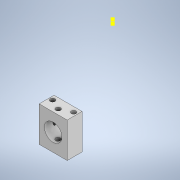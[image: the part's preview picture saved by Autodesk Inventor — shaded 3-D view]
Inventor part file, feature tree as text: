
AUTODESK INVENTOR PART (.ipt)
format: ipt  version: 2022 (Build 260153000, 153)  size: 735,744 bytes
history: native  units: in
note: dims shown in document units (in); Inventor stores cm internally (conversion verified against a paired STEP export)
features: sketch x33, extrude x30, projected_geometry x20, chamfer x7
ambient origin geometry x8: Origin, YZ Plane, XZ Plane, XY Plane, X Axis, Y Axis, Z Axis, Center Point
bodies: Solid1 (feature_tree)
feature tree (90):
  extrude  "Extrusion1"  TaperAngle=75.0deg  [1 undecoded]
  extrude  "Extrusion2"  Depth=0.0787in TaperAngle=0.0deg
  chamfer  "Chamfer1"  Distance=0.1181in
  chamfer  "Chamfer2"  Distance=0.0787in Angle=45.0deg
  chamfer  "Chamfer3"  Distance=0.0787in Angle=45.0deg
  extrude  "Extrusion3"  Depth=0.0787in
  extrude  "Extrusion4"  Depth=0.0787in
  extrude  "Extrusion5"  Depth=0.0787in TaperAngle=0.0deg
  extrude  "Extrusion6"  Depth=0.0787in TaperAngle=0.0deg
  extrude  "Extrusion7"  Depth=2.7559in
  chamfer  "Chamfer4"  Distance=0.3543in
  extrude  "Extrusion8"  Depth=0.3937in
  extrude  "Extrusion16"  Depth=0.3937in
  extrude  "Extrusion17"  Depth=0.3937in
  extrude  "Extrusion18"  Depth=0.3937in
  extrude  "Extrusion19"  Depth=0.3937in TaperAngle=0.0deg
  chamfer  "Chamfer7"  Distance=1.378in
  chamfer  "Chamfer8"  Distance=1.378in
  extrude  "Extrusion20"  Depth=0.3937in TaperAngle=0.0deg
  extrude  "Extrusion21"  Depth=0.3937in TaperAngle=0.0deg
  extrude  "Extrusion22"  Depth=0.3937in
  sketch  "Sketch25"  dims[d40=0.7874in]
  extrude  "Extrusion23"  Depth=0.3937in
  extrude  "Extrusion24"  Depth=0.3937in
  sketch  "Sketch28"  dims[d42=0.894in]
  extrude  "Extrusion27"  Depth=0.3937in
  extrude  "Extrusion28"  Depth=0.3937in
  extrude  "Extrusion29"  Depth=0.3937in
  extrude  "Extrusion30"  Depth=0.3937in TaperAngle=0.0deg
  extrude  "Extrusion31"  Depth=0.3937in TaperAngle=0.0deg
  chamfer  "Chamfer9"  Distance=0.0787in Angle=45.0deg
  extrude  "Extrusion32"  Depth=0.0787in TaperAngle=45.0deg
  extrude  "Extrusion33"  Depth=0.3937in
  extrude  "Extrusion34"  Depth=0.3937in TaperAngle=0.0deg
  extrude  "Extrusion35"  Depth=0.0787in
  extrude  "Extrusion36"  Depth=0.0787in
  sketch  "Sketch52"  dims[d53=0.2756in]
  sketch  "Sketch53"  dims[d54=0.2657in]
  extrude  "Extrusion37"  Depth=0.0787in
  extrude  "Extrusion38"  Depth=0.0787in
  extrude  "Extrusion39"  Depth=0.3937in TaperAngle=0.0deg
  sketch  "Sketch1"  dims[d0=3.1496in d4=75.0deg]
  sketch  "Sketch2"  dims[d5=0.1575in d6=2.7559in d7=0.0in d8=0.1181in d9=0.0in d10=0.1969in d11=0.0787in d12=45.0deg d13=0.1181in d14=0.0787in d15=45.0deg]
  projected_geometry  "Projected Loop1"
  sketch  "Sketch3"  dims[d16=0.1181in d17=0.0787in d18=45.0deg d19=0.0787in]
  sketch  "Sketch4"  dims[d20=0.0787in d22=0.0787in]
  sketch  "Sketch5"  dims[d23=0.0787in d24=0.1969in d25=0.0in]
  sketch  "Sketch7"  dims[d26=0.0787in d27=0.5906in d28=0.0in]
  sketch  "Sketch8"  dims[d29=1.5748in d30=2.7559in]
  sketch  "Sketch9"  dims[d31=0.7874in]
  sketch  "Sketch17"  dims[d32=0.8858in]
  projected_geometry  "Projected Loop4"
  sketch  "Sketch18"  dims[d33=1.5748in]
  sketch  "Sketch19"  dims[d34=1.7717in]
  sketch  "Sketch20"  dims[d35=1.1811in]
  projected_geometry  "Projected Loop5"
  sketch  "Sketch21"  dims[d36=0.7874in]
  projected_geometry  "Projected Loop6"
  sketch  "Sketch22"  dims[d37=0.0787in]
  projected_geometry  "Projected Loop7"
  sketch  "Sketch23"  dims[d38=0.7874in]
  projected_geometry  "Projected Loop8"
  projected_geometry  "Projected Loop9"
  projected_geometry  "Projected Loop10"
  projected_geometry  "Projected Loop11"
  projected_geometry  "Projected Loop12"
  sketch  "Sketch24"  dims[d39=0.0787in]
  projected_geometry  "Projected Loop13"
  sketch  "Sketch26"  dims[d41=0.9115in]
  projected_geometry  "Projected Loop14"
  sketch  "Sketch37"  dims[d43=0.1181in]
  projected_geometry  "Projected Loop18"
  sketch  "Sketch38"  dims[d44=0.1181in]
  projected_geometry  "Projected Loop19"
  sketch  "Sketch40"  dims[d45=1.5748in]
  projected_geometry  "Projected Loop20"
  sketch  "Sketch42"  dims[d46=0.0in]
  projected_geometry  "Projected Loop21"
  sketch  "Sketch43"  dims[d47=1.0787in]
  projected_geometry  "Projected Loop22"
  sketch  "Sketch46"  dims[d48=1.3386in]
  sketch  "Sketch48"  dims[d49=0.5197in]
  sketch  "Sketch49"  dims[d50=1.0787in]
  sketch  "Sketch50"  dims[d51=0.0in]
  sketch  "Sketch51"  dims[d52=0.0787in]
  projected_geometry  "Projected Loop23"
  sketch  "Sketch54"  dims[d55=0.5315in d56=0.3543in d57=0.0in]
  projected_geometry  "Projected Loop24"
  sketch  "Sketch55"  dims[d58=0.0394in d59=0.0787in d60=45.0deg d61=0.5709in d62=1.1417in d63=0.1575in d64=0.1575in d65=39.3307in d66=0.0in d106=1.378in d107=1.378in d108=0.1181in d109=0.0in d110=2.874in d111=0.0in d112=0.5906in d113=0.5906in d114=0.5906in d115=0.5906in d116=1.1811in d117=0.1181in d118=2.874in d119=0.0in d120=2.874in d121=0.0in d122=0.1181in d123=0.0787in d124=45.0deg d125=0.1181in d126=0.0787in d127=45.0deg d128=0.7421in d129=0.1181in d130=0.0in d131=0.0787in d132=0.0787in d133=0.0787in d134=0.0787in d135=7.874in d136=0.0in d137=0.3937in d138=0.0in d139=0.8169in d140=0.0in d141=0.8169in d142=0.0in d147=0.0098in d148=0.0in d149=0.0098in d150=0.0in d151=0.0098in d152=0.0in d153=0.0984in d154=0.7874in d155=0.0in d156=0.0984in d157=0.7874in d158=0.0in d159=0.1181in d160=0.0787in d161=45.0deg d162=0.1181in d163=1.5748in d165=360.0deg d167=0.5906in d168=0.0in d170=1.5748in d171=0.1181in d172=360.0deg d173=0.5906in d174=0.0in d175=0.3543in d176=0.1575in d177=0.1575in d178=1.378in d179=0.0in d180=0.0in d181=0.0in d182=0.3937in d183=0.0in d185=0.3346in d186=1.1811in d187=0.0in d188=0.0in d189=0.0in d190=0.5906in d191=0.0in d192=0.0in]
  projected_geometry  "Projected Loop25"
note: 1 required parameter value undecoded (feature->parameter linkage not recoverable at this tier; creation-order binding heuristic only, values carry confidence <= 0.55)
